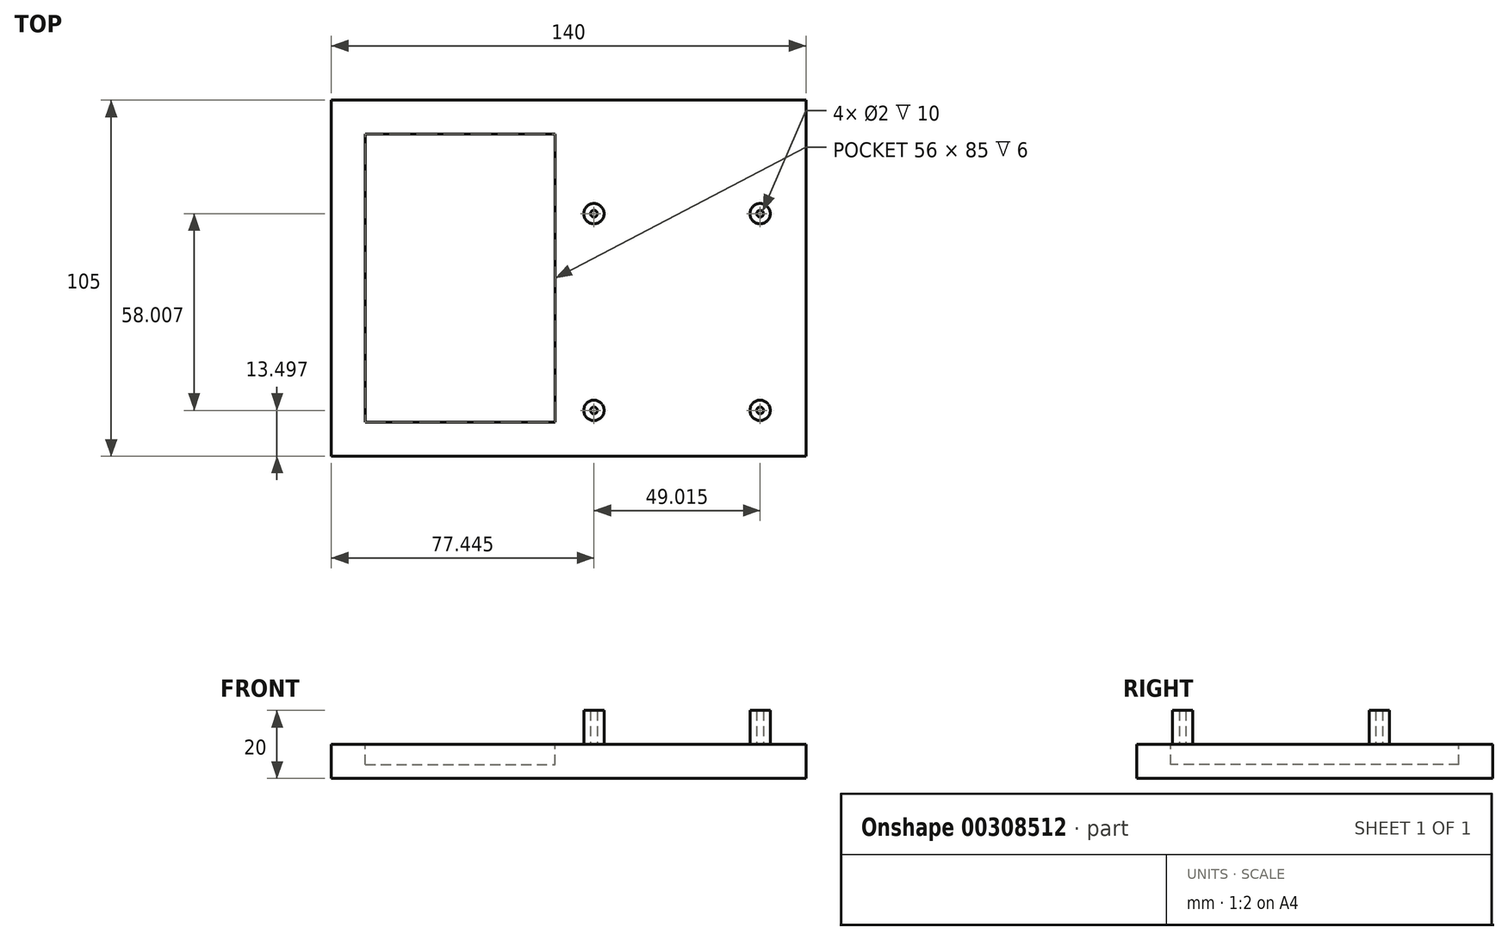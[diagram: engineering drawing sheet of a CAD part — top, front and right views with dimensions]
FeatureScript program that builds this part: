
annotation { "Feature Type Name" : "Feature", "Feature Type Description" : "" }
export const myFeature = defineFeature(function(context is Context, id is Id, definition is map)
    precondition{}
    {
        {
            var Q0;
            Q0=qCreatedBy(makeId("Top.planeOp"),FACE);
            var sketch = newSketch(context, id + "F0", { "sketchPlane" : qUnion([Q0])});
            skLineSegment(sketch, "E0.bottom", {"start": v(0, 0) * mm, "end": v(140, 0) * mm});
            skLineSegment(sketch, "E0.top", {"start": v(0, 105) * mm, "end": v(140, 105) * mm});
            skLineSegment(sketch, "E0.left", {"start": v(0, 0) * mm, "end": v(0, 105) * mm});
            skLineSegment(sketch, "E0.right", {"start": v(140, 0) * mm, "end": v(140, 105) * mm});
            skSolve(sketch);
        }
        {
            var Q0;
            Q0=makeQuery(id+"F0.imprint","IMPRINT",FACE,{"disambiguationData":[TD([[makeQuery(id+"F0.imprint","IMPRINT",EDGE,{"derivedFrom":sQuery(id+"F0.wireOp",EDGE,"E0.bottom")}),1.0]])]});
            extrude(context, id + "F1", {"entities" : qUnion([Q0]), "oppositeDirection" : true, "depth" : 10 * mm});
        }
        {
            var Q0;
            Q0=qCreatedBy(makeId("Top.planeOp"),FACE);
            var sketch = newSketch(context, id + "F2", { "sketchPlane" : qUnion([Q0])});
            skCircle(sketch, "E1", {"center": v(126.46, 13.5) * mm, "radius": 3 * mm});
            skCircle(sketch, "E2", {"center": v(126.46, 13.5) * mm, "radius": 1 * mm});
            skCircle(sketch, "E3", {"center": v(77.44, 13.5) * mm, "radius": 3 * mm});
            skCircle(sketch, "E4", {"center": v(77.44, 13.5) * mm, "radius": 1 * mm});
            skCircle(sketch, "E5", {"center": v(126.46, 71.5) * mm, "radius": 3 * mm});
            skCircle(sketch, "E6", {"center": v(126.46, 71.5) * mm, "radius": 1 * mm});
            skCircle(sketch, "E7", {"center": v(77.44, 71.5) * mm, "radius": 3 * mm});
            skCircle(sketch, "E8", {"center": v(77.44, 71.5) * mm, "radius": 1 * mm});
            skSolve(sketch);
        }
        {
            var Q0;
            Q0=makeQuery(id+"F2.imprint","IMPRINT",FACE,{"disambiguationData":[TD([[makeQuery(id+"F2.imprint","IMPRINT",EDGE,{"derivedFrom":sQuery(id+"F2.wireOp",EDGE,"E7")}),1.0]])]});
            var Q1;
            Q1=makeQuery(id+"F2.imprint","IMPRINT",FACE,{"disambiguationData":[TD([[makeQuery(id+"F2.imprint","IMPRINT",EDGE,{"derivedFrom":sQuery(id+"F2.wireOp",EDGE,"E5")}),1.0]])]});
            var Q2;
            Q2=makeQuery(id+"F2.imprint","IMPRINT",FACE,{"disambiguationData":[TD([[makeQuery(id+"F2.imprint","IMPRINT",EDGE,{"derivedFrom":sQuery(id+"F2.wireOp",EDGE,"E1")}),1.0]])]});
            var Q3;
            Q3=makeQuery(id+"F2.imprint","IMPRINT",FACE,{"disambiguationData":[TD([[makeQuery(id+"F2.imprint","IMPRINT",EDGE,{"derivedFrom":sQuery(id+"F2.wireOp",EDGE,"E3")}),1.0]])]});
            extrude(context, id + "F3", {"entities" : qUnion([Q0, Q1, Q2, Q3]), "operationType" : NewBodyOperationType.ADD, "depth" : 10 * mm});
        }
        {
            var Q0;
            {var subQ0=sQuery(id+"F0.wireOp",EDGE,"E0.left");var subQ1=sQuery(id+"F0.wireOp",EDGE,"E0.top");var subQ2=sQuery(id+"F0.wireOp",EDGE,"E0.right");var subQ3=sQuery(id+"F0.wireOp",EDGE,"E0.bottom");Q0=makeQuery(id+"F3.boolean.opBoolean","SPLIT",FACE,{"disambiguationData":[TD([makeQuery(id+"F1.opExtrude","SWEPT_FACE",FACE,{"disambiguationData":[OSD([subQ3])]})])],"derivedFrom":makeQuery(id+"F1.opExtrude","CAP_FACE",FACE,{"disambiguationData":[OSD([subQ3,subQ1,subQ0,subQ2])],"isStart":true})});}
            var sketch = newSketch(context, id + "F4", { "sketchPlane" : qUnion([Q0])});
            skLineSegment(sketch, "E9", {"start": v(10, 10) * mm, "end": v(66, 10) * mm});
            skLineSegment(sketch, "E10", {"start": v(66, 10) * mm, "end": v(66, 95) * mm});
            skLineSegment(sketch, "E11", {"start": v(66, 95) * mm, "end": v(10, 95) * mm});
            skLineSegment(sketch, "E12", {"start": v(10, 95) * mm, "end": v(10, 10) * mm});
            skSolve(sketch);
        }
        {
            var Q0;
            Q0=makeQuery(id+"F4.imprint","IMPRINT",FACE,{"disambiguationData":[TD([[makeQuery(id+"F4.imprint","IMPRINT",EDGE,{"derivedFrom":sQuery(id+"F4.wireOp",EDGE,"E9")}),1.0]])]});
            extrude(context, id + "F5", {"entities" : qUnion([Q0]), "operationType" : NewBodyOperationType.REMOVE, "oppositeDirection" : true, "depth" : 6 * mm});
        }
    });
